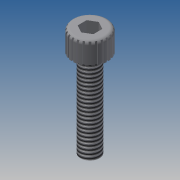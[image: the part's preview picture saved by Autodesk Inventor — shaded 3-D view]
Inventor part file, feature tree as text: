
AUTODESK INVENTOR PART (.ipt)
format: ipt  version: 2014 SP1 (Build 180222100, 222)  size: 242,176 bytes
history: native  units: in
note: dims shown in document units (in); Inventor stores cm internally (conversion verified against a paired STEP export)
features: sketch x5, extrude x4, fillet x1, thread x1, plane x1, pattern_circular x1
ambient origin geometry x8: Origin, YZ Plane, XZ Plane, XY Plane, X Axis, Y Axis, Z Axis, Center Point
bodies: Solid1 (feature_tree)
feature tree (13):
  extrude  "Extrusion1"  Depth=0.18in TaperAngle=0.0deg
  extrude  "Extrusion2"  Depth=0.03in
  fillet  "Fillet1"  Radius=0.162in
  extrude  "Extrusion3"  Depth=0.015in TaperAngle=0.0deg
  thread  "Thread3"  [1 undecoded]
  sketch  "Sketch4"  dims[d16=0.01in d17=0.0in d18=9.4488in d19=360.0deg]
  plane  "Work Plane1"
  extrude  "Extrusion4"  Depth=9.4488in TaperAngle=360.0deg
  pattern_circular  "Circular Pattern1"  [2 undecoded]
  sketch  "Sketch1"  dims[d0=0.3in d1=0.18in d2=0.0in]
  sketch  "Sketch2"  dims[d3=0.1in d4=0.0in d5=0.03in d6=0.162in]
  sketch  "Sketch3"  dims[d7=0.75in d8=0.0in d13=1.0in d14=0.0in d15=0.015in]
  sketch  "Sketch5"
note: 3 required parameter values undecoded (feature->parameter linkage not recoverable at this tier; creation-order binding heuristic only, values carry confidence <= 0.55)
